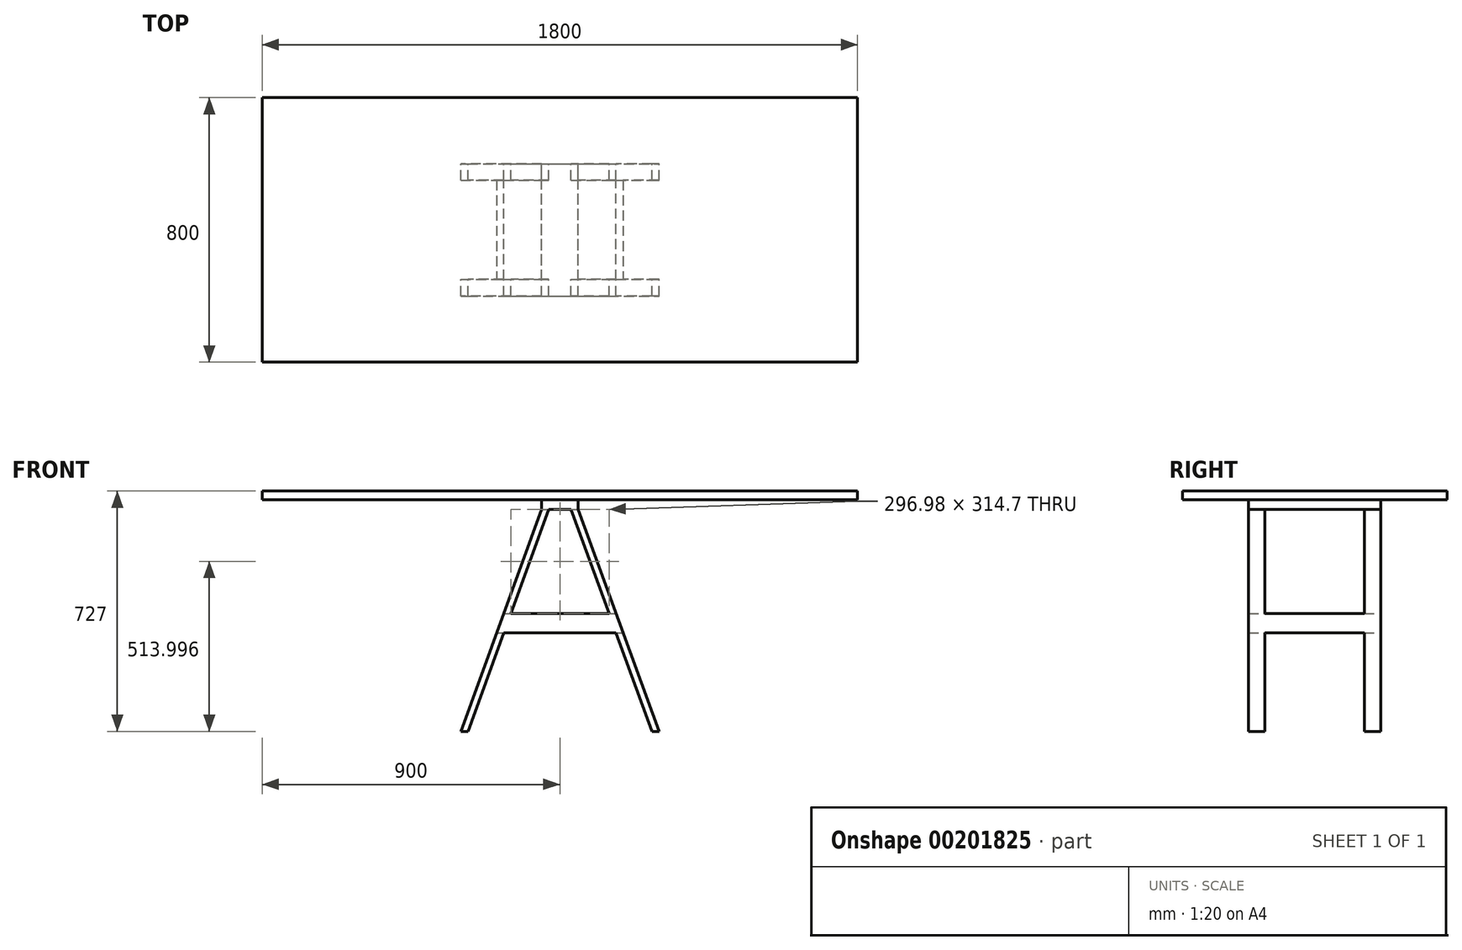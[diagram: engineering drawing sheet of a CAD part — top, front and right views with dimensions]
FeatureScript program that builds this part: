
annotation { "Feature Type Name" : "Feature", "Feature Type Description" : "" }
export const myFeature = defineFeature(function(context is Context, id is Id, definition is map)
    precondition{}
    {
        {
            var Q0;
            Q0=qCreatedBy(makeId("Top.planeOp"),FACE);
            var sketch = newSketch(context, id + "F0", { "sketchPlane" : qUnion([Q0])});
            skLineSegment(sketch, "E0.bottom", {"start": v(900, -400) * mm, "end": v(-900, -400) * mm});
            skLineSegment(sketch, "E0.top", {"start": v(900, 400) * mm, "end": v(-900, 400) * mm});
            skLineSegment(sketch, "E0.left", {"start": v(900, -400) * mm, "end": v(900, 400) * mm});
            skLineSegment(sketch, "E0.right", {"start": v(-900, -400) * mm, "end": v(-900, 400) * mm});
            skPoint(sketch, "E0.middle", {"position": v(0, 0) * mm});
            skSolve(sketch);
        }
        {
            var Q0;
            Q0=makeQuery(id+"F0.imprint","IMPRINT",FACE,{"disambiguationData":[TD([[makeQuery(id+"F0.imprint","IMPRINT",EDGE,{"derivedFrom":sQuery(id+"F0.wireOp",EDGE,"E0.bottom")}),-1.0]])]});
            extrude(context, id + "F1", {"entities" : qUnion([Q0]), "depth" : 27 * mm});
        }
        {
            var Q0;
            Q0=qCreatedBy(makeId("Front.planeOp"),FACE);
            var sketch = newSketch(context, id + "F2", { "sketchPlane" : qUnion([Q0])});
            skLineSegment(sketch, "E1.bottom", {"start": v(-55.23, 0) * mm, "end": v(55.23, 0) * mm});
            skLineSegment(sketch, "E1.top", {"start": v(-55.23, -28.66) * mm, "end": v(55.23, -28.66) * mm});
            skLineSegment(sketch, "E1.left", {"start": v(-55.23, 0) * mm, "end": v(-55.23, -28.66) * mm});
            skLineSegment(sketch, "E1.right", {"start": v(55.23, 0) * mm, "end": v(55.23, -28.66) * mm});
            skLineSegment(sketch, "E2", {"start": v(55.23, -28.66) * mm, "end": v(299.58, -700) * mm});
            skLineSegment(sketch, "E3", {"start": v(299.58, -700) * mm, "end": v(278.3, -700) * mm});
            skLineSegment(sketch, "E4", {"start": v(278.3, -700) * mm, "end": v(33.95, -28.66) * mm});
            skLineSegment(sketch, "E5", {"start": v(0, 0) * mm, "end": v(0, -651.88) * mm, "construction": true});
            skPoint(sketch, "E5.endSnap0", {"position": v(0, -28.66) * mm});
            skLineSegment(sketch, "E6.MirrorCS", {"start": v(-278.3, -700) * mm, "end": v(-33.95, -28.66) * mm});
            skLineSegment(sketch, "E7.MirrorCS", {"start": v(-55.23, -28.66) * mm, "end": v(-299.58, -700) * mm});
            skLineSegment(sketch, "E8.MirrorCS", {"start": v(-299.58, -700) * mm, "end": v(-278.3, -700) * mm});
            skLineSegment(sketch, "E9.bottom", {"start": v(-169.77, -343.35) * mm, "end": v(169.77, -343.35) * mm});
            skLineSegment(sketch, "E9.top", {"start": v(-169.77, -401.83) * mm, "end": v(169.77, -401.83) * mm});
            skLineSegment(sketch, "E9.left", {"start": v(-169.77, -343.35) * mm, "end": v(-169.77, -401.83) * mm});
            skLineSegment(sketch, "E9.right", {"start": v(169.77, -343.35) * mm, "end": v(169.77, -401.83) * mm});
            skSolve(sketch);
        }
        {
            var Q0;
            {var subQ0=sQuery(id+"F2.wireOp",EDGE,"E8.MirrorCS");Q0=makeQuery(id+"F2.imprint","IMPRINT",FACE,{"disambiguationData":[TD([[makeQuery(id+"F2.imprint","IMPRINT",EDGE,{"derivedFrom":subQ0}),1.0]])]});}
            var Q1;
            {var subQ1=sQuery(id+"F2.wireOp",EDGE,"E1.top");var subQ3=sQuery(id+"F2.wireOp",EDGE,"E6.MirrorCS");var subQ4=makeQuery(id+"F2.imprint","INTERSECT",VERTEX,{"derivedFrom":[subQ1,subQ3]});Q1=makeQuery(id+"F2.imprint","IMPRINT",FACE,{"disambiguationData":[TD([[makeQuery(id+"F2.imprint","IMPRINT",EDGE,{"disambiguationData":[TD([[subQ4,1.0]])],"derivedFrom":subQ3}),1.0]])]});}
            var Q2;
            {var subQ0=sQuery(id+"F2.wireOp",EDGE,"E9.left");Q2=makeQuery(id+"F2.imprint","IMPRINT",FACE,{"disambiguationData":[TD([[makeQuery(id+"F2.imprint","IMPRINT",EDGE,{"derivedFrom":subQ0}),1.0]])]});}
            var Q3;
            Q3=makeQuery(id+"F2.imprint","IMPRINT",FACE,{"disambiguationData":[TD([[makeQuery(id+"F2.imprint","IMPRINT",EDGE,{"derivedFrom":sQuery(id+"F2.wireOp",EDGE,"E1.bottom")}),-1.0]])]});
            var Q4;
            {var subQ1=sQuery(id+"F2.wireOp",EDGE,"E1.top");var subQ3=sQuery(id+"F2.wireOp",EDGE,"E4");var subQ4=makeQuery(id+"F2.imprint","INTERSECT",VERTEX,{"derivedFrom":[subQ1,subQ3]});Q4=makeQuery(id+"F2.imprint","IMPRINT",FACE,{"disambiguationData":[TD([[makeQuery(id+"F2.imprint","IMPRINT",EDGE,{"disambiguationData":[TD([[subQ4,1.0]])],"derivedFrom":subQ3}),-1.0]])]});}
            var Q5;
            {var subQ0=sQuery(id+"F2.wireOp",EDGE,"E9.right");Q5=makeQuery(id+"F2.imprint","IMPRINT",FACE,{"disambiguationData":[TD([[makeQuery(id+"F2.imprint","IMPRINT",EDGE,{"derivedFrom":subQ0}),-1.0]])]});}
            var Q6;
            {var subQ0=sQuery(id+"F2.wireOp",EDGE,"E3");Q6=makeQuery(id+"F2.imprint","IMPRINT",FACE,{"disambiguationData":[TD([[makeQuery(id+"F2.imprint","IMPRINT",EDGE,{"derivedFrom":subQ0}),-1.0]])]});}
            var Q7;
            {var subQ0=sQuery(id+"F2.wireOp",EDGE,"E9.top");Q7=makeQuery(id+"F2.imprint","IMPRINT",FACE,{"disambiguationData":[TD([[makeQuery(id+"F2.imprint","IMPRINT",EDGE,{"derivedFrom":subQ0}),1.0]])]});}
            extrude(context, id + "F3", {"entities" : qUnion([Q0, Q1, Q2, Q3, Q4, Q5, Q6, Q7]), "depth" : 400 * mm, "symmetric" : true});
        }
        {
            var Q0;
            Q0=qCreatedBy(makeId("Right.planeOp"),FACE);
            var sketch = newSketch(context, id + "F4", { "sketchPlane" : qUnion([Q0])});
            skLineSegment(sketch, "E10.bottom", {"start": v(-150, -700) * mm, "end": v(150, -700) * mm});
            skLineSegment(sketch, "E10.top", {"start": v(-150, -28.66) * mm, "end": v(150, -28.66) * mm});
            skLineSegment(sketch, "E10.left", {"start": v(-150, -700) * mm, "end": v(-150, -28.66) * mm});
            skLineSegment(sketch, "E10.right", {"start": v(150, -700) * mm, "end": v(150, -28.66) * mm});
            skLineSegment(sketch, "E11.top", {"start": v(-150, -343.35) * mm, "end": v(150, -343.35) * mm});
            skLineSegment(sketch, "E11.left", {"start": v(-150, -28.66) * mm, "end": v(-150, -343.35) * mm});
            skLineSegment(sketch, "E11.right", {"start": v(150, -28.66) * mm, "end": v(150, -343.35) * mm});
            skLineSegment(sketch, "E12.bottom", {"start": v(150, -401.83) * mm, "end": v(-150, -401.83) * mm});
            skLineSegment(sketch, "E12.top", {"start": v(150, -700) * mm, "end": v(-150, -700) * mm});
            skLineSegment(sketch, "E12.left", {"start": v(150, -401.83) * mm, "end": v(150, -700) * mm});
            skLineSegment(sketch, "E12.right", {"start": v(-150, -401.83) * mm, "end": v(-150, -700) * mm});
            skSolve(sketch);
        }
        {
            var Q0;
            Q0=makeQuery(id+"F4.imprint","IMPRINT",FACE,{"disambiguationData":[TD([[makeQuery(id+"F4.imprint","IMPRINT",EDGE,{"derivedFrom":sQuery(id+"F4.wireOp",EDGE,"E10.top")}),-1.0]])]});
            var Q1;
            Q1=makeQuery(id+"F4.imprint","IMPRINT",FACE,{"disambiguationData":[TD([[makeQuery(id+"F4.imprint","IMPRINT",EDGE,{"derivedFrom":sQuery(id+"F4.wireOp",EDGE,"E12.bottom")}),1.0]])]});
            extrude(context, id + "F5", {"entities" : qUnion([Q0, Q1]), "operationType" : NewBodyOperationType.REMOVE, "endBound" : BoundingType.THROUGH_ALL, "oppositeDirection" : true, "depth" : 25 * mm, "hasSecondDirection" : true, "secondDirectionBound" : BoundingType.THROUGH_ALL, "secondDirectionOppositeDirection" : false, "secondDirectionDepth" : 25 * mm});
        }
    });
